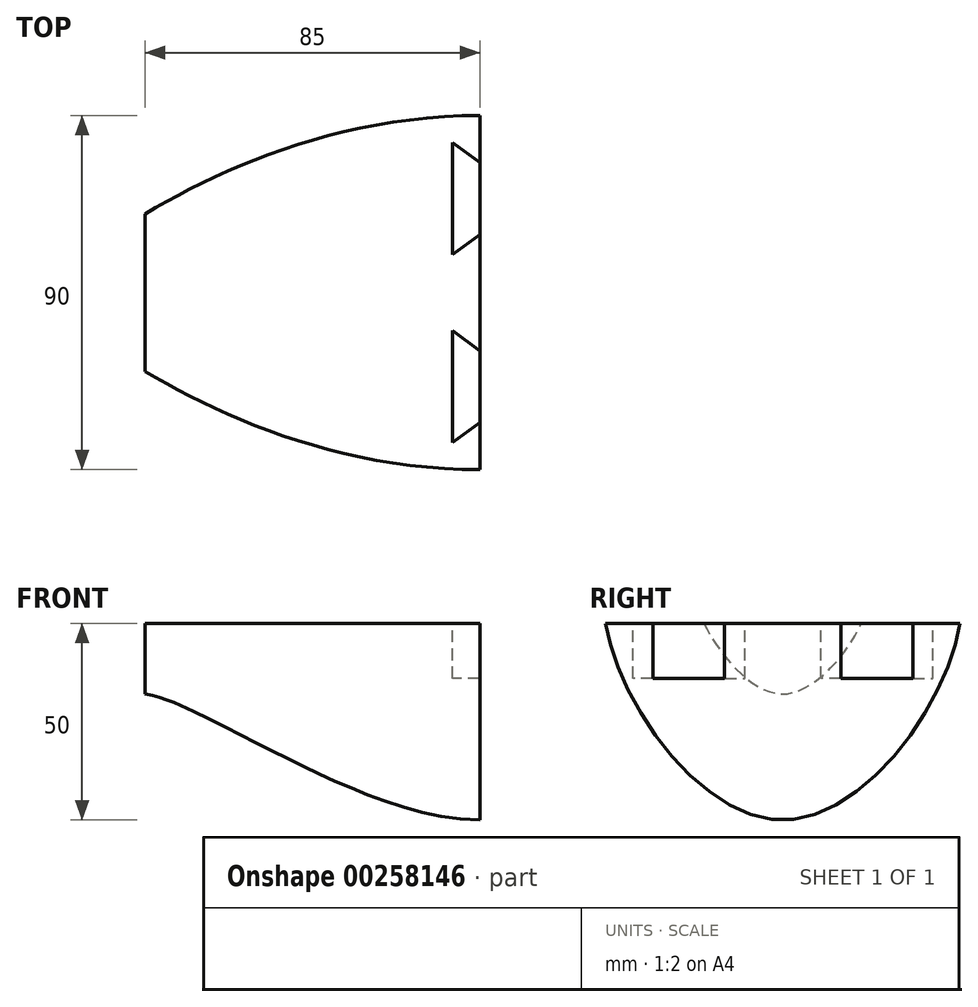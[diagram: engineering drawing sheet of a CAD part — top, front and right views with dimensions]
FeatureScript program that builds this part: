
annotation { "Feature Type Name" : "Feature", "Feature Type Description" : "" }
export const myFeature = defineFeature(function(context is Context, id is Id, definition is map)
    precondition{}
    {
        {
            var Q0;
            Q0=qCreatedBy(makeId("Right.planeOp"),FACE);
            cPlane(context, id + "F0", {"entities" : qUnion([Q0]), "cplaneType" : CPlaneType.OFFSET, "offset" : 85 * mm, "oppositeDirection" : true, "width" : 150 * mm, "height" : 150 * mm});
        }
        {
            var Q0;
            Q0=qCreatedBy(makeId("Right.planeOp"),FACE);
            var sketch = newSketch(context, id + "F1", { "sketchPlane" : qUnion([Q0])});
            skFitSpline(sketch, "E0", {"points": [v(-45, 0) * mm, v(0, -50) * mm, v(45, 0) * mm], "startDerivative": vector(18, -120) * mm, "endDerivative": vector(18, 120) * mm});
            skFitSpline(sketch, "E1", {"points": [v(-45, 0) * mm, v(0, 0) * mm], "startDerivative": vector(54.38, 0) * mm, "endDerivative": vector(54.38, 0) * mm});
            skFitSpline(sketch, "E2", {"points": [v(0, 0) * mm, v(45, 0) * mm], "startDerivative": vector(45, 0) * mm, "endDerivative": vector(45, 0) * mm});
            skSolve(sketch);
        }
        {
            var Q0;
            Q0=qCreatedBy(id+"F0.planeOp",FACE);
            var sketch = newSketch(context, id + "F2", { "sketchPlane" : qUnion([Q0])});
            skFitSpline(sketch, "E3", {"points": [v(-20, 0) * mm, v(0, -18) * mm, v(20, 0) * mm], "startDerivative": vector(12, -30) * mm, "endDerivative": vector(12, 30) * mm});
            skFitSpline(sketch, "E4", {"points": [v(0, 0) * mm, v(-20, 0) * mm], "startDerivative": vector(-19.03, 0) * mm, "endDerivative": vector(-19.03, 0) * mm});
            skFitSpline(sketch, "E5", {"points": [v(0, 0) * mm, v(20, 0) * mm], "startDerivative": vector(20, 0) * mm, "endDerivative": vector(20, 0) * mm});
            skSolve(sketch);
        }
        {
            var Q0;
            Q0=qCreatedBy(makeId("Front.planeOp"),FACE);
            var sketch = newSketch(context, id + "F3", { "sketchPlane" : qUnion([Q0])});
            skPoint(sketch, "E6.0", {"position": v(-85, -18) * mm});
            skPoint(sketch, "E7.0", {"position": v(0, -50) * mm});
            skFitSpline(sketch, "E8", {"points": [v(-85, -18) * mm, v(0, -50) * mm], "startDerivative": vector(45, -6) * mm, "endDerivative": vector(89.92, 0) * mm});
            skSolve(sketch);
        }
        {
            var Q0;
            Q0=qCreatedBy(makeId("Top.planeOp"),FACE);
            var sketch = newSketch(context, id + "F4", { "sketchPlane" : qUnion([Q0])});
            skPoint(sketch, "E9.0", {"position": v(-85, 20) * mm});
            skPoint(sketch, "E10.0", {"position": v(0, 45) * mm});
            skPoint(sketch, "E11.0", {"position": v(-85, -20) * mm});
            skPoint(sketch, "E12.0", {"position": v(0, -45) * mm});
            skFitSpline(sketch, "E13", {"points": [v(-85, 20) * mm, v(0, 45) * mm], "startDerivative": vector(60, 36) * mm, "endDerivative": vector(105, 0) * mm});
            skFitSpline(sketch, "E14.MirrorCS", {"points": [v(-85, -20) * mm, v(0, -45) * mm], "startDerivative": vector(60, -36) * mm, "endDerivative": vector(105, 0) * mm});
            skSolve(sketch);
        }
        {
            var Q0;
            Q0=makeQuery(id+"F1.imprint","IMPRINT",FACE,{"disambiguationData":[TD([[makeQuery(id+"F1.imprint","IMPRINT",EDGE,{"derivedFrom":sQuery(id+"F1.wireOp",EDGE,"E0")}),1.0]])]});
            var Q1;
            Q1=makeQuery(id+"F2.imprint","IMPRINT",FACE,{"disambiguationData":[TD([[makeQuery(id+"F2.imprint","IMPRINT",EDGE,{"derivedFrom":sQuery(id+"F2.wireOp",EDGE,"E3")}),1.0]])]});
            var Q2;
            Q2=sQuery(id+"F3.wireOp",EDGE,"E8");
            var Q3;
            Q3=sQuery(id+"F4.wireOp",EDGE,"E14.MirrorCS");
            var Q4;
            Q4=sQuery(id+"F4.wireOp",EDGE,"E13");
            loft(context, id + "F5", {"addGuides" : true, "sheetProfilesArray" : [{ "sheetProfileEntities" : qUnion([Q0]) }, { "sheetProfileEntities" : qUnion([Q1]) }], "guidesArray" : [{ "guideEntities" : qUnion([Q2]), "guideDerivativeType" : LoftGuideDerivativeType.DEFAULT, "guideDerivativeMagnitude" : 1 }, { "guideEntities" : qUnion([Q3]), "guideDerivativeType" : LoftGuideDerivativeType.DEFAULT, "guideDerivativeMagnitude" : 1 }, { "guideEntities" : qUnion([Q4]), "guideDerivativeType" : LoftGuideDerivativeType.DEFAULT, "guideDerivativeMagnitude" : 1 }]});
        }
        {
            var Q0;
            Q0=makeQuery(id+"F5.opLoft","SWEPT_FACE",FACE,{"disambiguationData":[OSD([sQuery(id+"F1.wireOp",EDGE,"E1"),sQuery(id+"F1.wireOp",EDGE,"E2"),sQuery(id+"F2.wireOp",EDGE,"E4"),sQuery(id+"F2.wireOp",EDGE,"E5"),sQuery(id+"F4.wireOp",EDGE,"E14.MirrorCS")])]});
            var sketch = newSketch(context, id + "F6", { "sketchPlane" : qUnion([Q0])});
            skPoint(sketch, "E15", {"position": v(0, 33) * mm});
            skPoint(sketch, "E16", {"position": v(-6.91, 38.14) * mm});
            skLineSegment(sketch, "E17", {"start": v(0, 33) * mm, "end": v(-6.91, 38.14) * mm});
            skLineSegment(sketch, "E18", {"start": v(-6.91, 38.14) * mm, "end": v(-6.91, 23.9) * mm});
            skLineSegment(sketch, "E19", {"start": v(0, 33) * mm, "end": v(0, 22.74) * mm});
            skLineSegment(sketch, "E20.MirrorCS", {"start": v(0, 14.8) * mm, "end": v(0, 22.74) * mm});
            skLineSegment(sketch, "E21.MirrorCS", {"start": v(-6.91, 9.65) * mm, "end": v(-6.91, 23.9) * mm});
            skLineSegment(sketch, "E22.MirrorCS", {"start": v(0, 14.8) * mm, "end": v(-6.91, 9.65) * mm});
            skLineSegment(sketch, "E23.MirrorCS", {"start": v(0, -33) * mm, "end": v(0, -22.74) * mm});
            skLineSegment(sketch, "E24.MirrorCS", {"start": v(0, -33) * mm, "end": v(-6.91, -38.14) * mm});
            skLineSegment(sketch, "E25.MirrorCS", {"start": v(0, -14.8) * mm, "end": v(0, -22.74) * mm});
            skLineSegment(sketch, "E26.MirrorCS", {"start": v(-6.91, -38.14) * mm, "end": v(-6.91, -23.9) * mm});
            skLineSegment(sketch, "E27.MirrorCS", {"start": v(-6.91, -9.65) * mm, "end": v(-6.91, -23.9) * mm});
            skLineSegment(sketch, "E28.MirrorCS", {"start": v(0, -14.8) * mm, "end": v(-6.91, -9.65) * mm});
            skSolve(sketch);
        }
        {
            var Q0;
            Q0=makeQuery(id+"F6.imprint","IMPRINT",FACE,{"disambiguationData":[TD([[makeQuery(id+"F6.imprint","IMPRINT",EDGE,{"derivedFrom":sQuery(id+"F6.wireOp",EDGE,"E23.MirrorCS")}),1.0]])]});
            var Q1;
            Q1=makeQuery(id+"F6.imprint","IMPRINT",FACE,{"disambiguationData":[TD([[makeQuery(id+"F6.imprint","IMPRINT",EDGE,{"derivedFrom":sQuery(id+"F6.wireOp",EDGE,"E17")}),1.0]])]});
            extrude(context, id + "F7", {"entities" : qUnion([Q0, Q1]), "operationType" : NewBodyOperationType.REMOVE, "oppositeDirection" : true, "depth" : 14 * mm});
        }
    });
